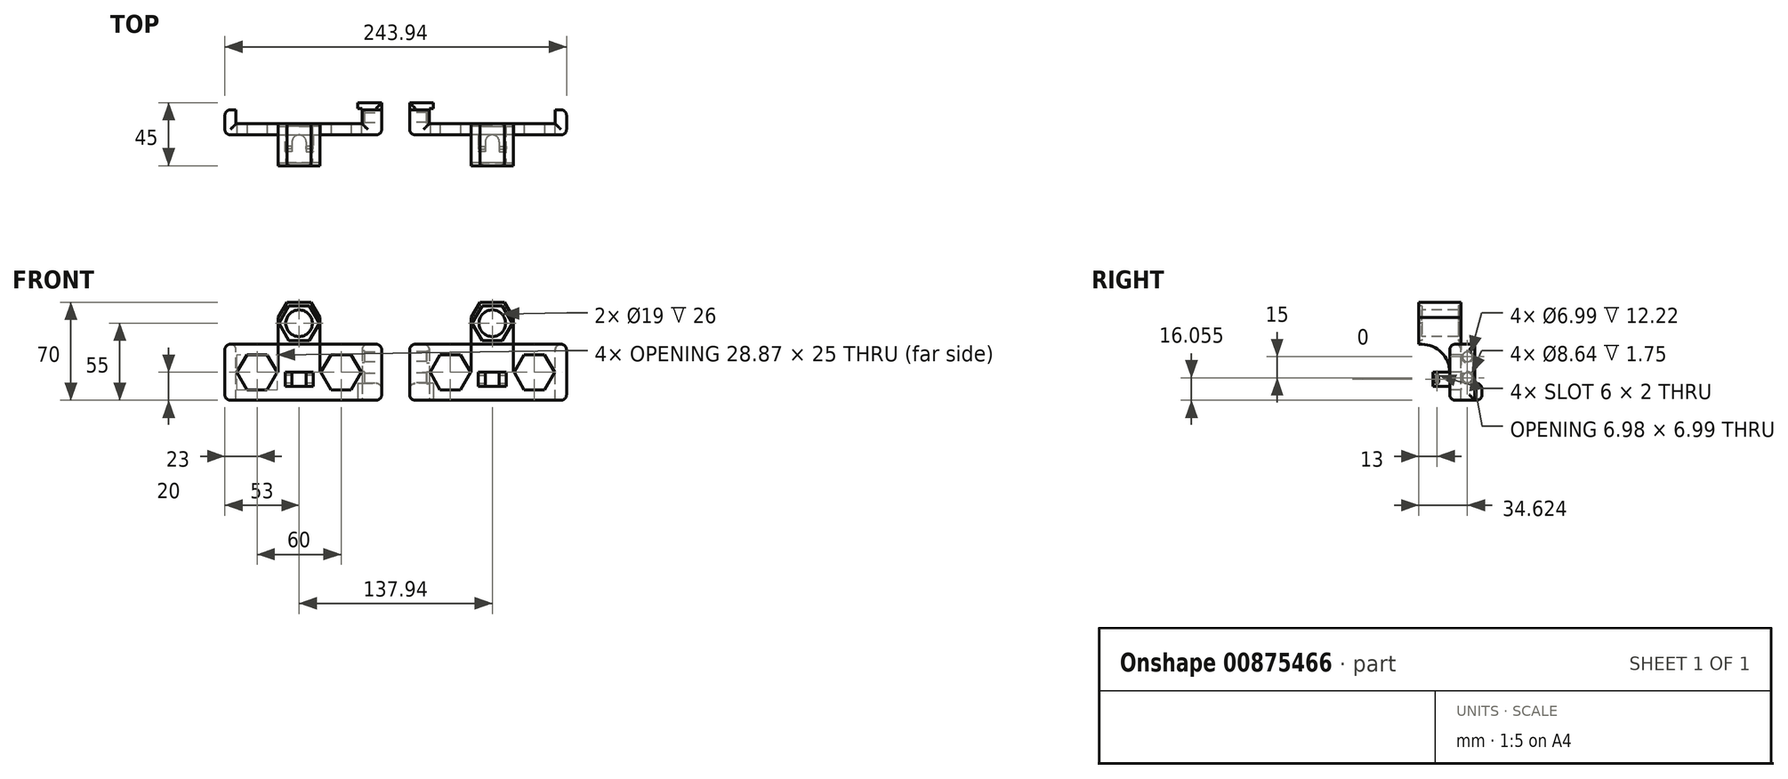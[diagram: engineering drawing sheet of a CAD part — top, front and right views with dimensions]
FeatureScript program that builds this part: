
annotation { "Feature Type Name" : "Feature", "Feature Type Description" : "" }
export const myFeature = defineFeature(function(context is Context, id is Id, definition is map)
    precondition{}
    {
        {
            var Q0;
            Q0=qCreatedBy(makeId("Front.planeOp"),FACE);
            var sketch = newSketch(context, id + "F0", { "sketchPlane" : qUnion([Q0])});
            skLineSegment(sketch, "E0.bottom", {"start": v(-53, 20) * mm, "end": v(53, 20) * mm});
            skLineSegment(sketch, "E0.top", {"start": v(-53, -20) * mm, "end": v(53, -20) * mm});
            skLineSegment(sketch, "E0.left", {"start": v(-53, 20) * mm, "end": v(-53, -20) * mm});
            skLineSegment(sketch, "E0.right", {"start": v(53, 20) * mm, "end": v(53, -20) * mm});
            skPoint(sketch, "E0.middle", {"position": v(0, 0) * mm});
            skSolve(sketch);
        }
        {
            var Q0;
            Q0=qSketchRegion(id+"F0",true);
            extrude(context, id + "F1", {"entities" : qUnion([Q0]), "depth" : 8 * mm, "offsetDistance" : 25 * mm});
        }
        {
            var Q0;
            Q0=makeQuery(id+"F1.opExtrude","CAP_FACE",FACE,{"disambiguationData":[OSD([sQuery(id+"F0.wireOp",EDGE,"E0.bottom"),sQuery(id+"F0.wireOp",EDGE,"E0.top"),sQuery(id+"F0.wireOp",EDGE,"E0.left"),sQuery(id+"F0.wireOp",EDGE,"E0.right")])],"isStart":true});
            var sketch = newSketch(context, id + "F2", { "sketchPlane" : qUnion([Q0])});
            skLineSegment(sketch, "E1.bottom", {"start": v(-53, 20) * mm, "end": v(-45, 20) * mm});
            skLineSegment(sketch, "E1.top", {"start": v(-53, -20) * mm, "end": v(-45, -20) * mm});
            skLineSegment(sketch, "E1.left", {"start": v(-53, 20) * mm, "end": v(-53, -20) * mm});
            skLineSegment(sketch, "E1.right", {"start": v(-45, 20) * mm, "end": v(-45, -20) * mm});
            skLineSegment(sketch, "E2.bottom", {"start": v(53, -20) * mm, "end": v(45, -20) * mm});
            skLineSegment(sketch, "E2.top", {"start": v(53, 20) * mm, "end": v(45, 20) * mm});
            skLineSegment(sketch, "E2.left", {"start": v(53, -20) * mm, "end": v(53, 20) * mm});
            skLineSegment(sketch, "E2.right", {"start": v(45, -20) * mm, "end": v(45, 20) * mm});
            skLineSegment(sketch, "E3.bottom", {"start": v(-53, 20) * mm, "end": v(-58.97, 20) * mm});
            skLineSegment(sketch, "E3.top", {"start": v(-53, -20) * mm, "end": v(-58.97, -20) * mm});
            skLineSegment(sketch, "E3.right", {"start": v(-58.97, 20) * mm, "end": v(-58.97, -20) * mm});
            skSolve(sketch);
        }
        {
            var Q0;
            Q0=qSketchRegion(id+"F2",true);
            extrude(context, id + "F3", {"entities" : qUnion([Q0]), "operationType" : NewBodyOperationType.ADD, "depth" : 10 * mm, "offsetDistance" : 25 * mm, "hasSecondDirection" : true, "secondDirectionOppositeDirection" : true, "secondDirectionDepth" : 8 * mm});
        }
        {
            var Q0;
            Q0=makeQuery(id+"F3.opExtrude","CAP_FACE",FACE,{"disambiguationData":[OSD([sQuery(id+"F2.wireOp",EDGE,"E1.bottom"),sQuery(id+"F2.wireOp",EDGE,"E1.top"),sQuery(id+"F2.wireOp",EDGE,"E1.left"),sQuery(id+"F2.wireOp",EDGE,"E1.right")])],"isStart":false});
            var sketch = newSketch(context, id + "F4", { "sketchPlane" : qUnion([Q0])});
            skLineSegment(sketch, "E4.bottom", {"start": v(-45, -20) * mm, "end": v(-58.97, -20) * mm});
            skLineSegment(sketch, "E4.top", {"start": v(-45, -8) * mm, "end": v(-58.97, -8) * mm});
            skLineSegment(sketch, "E4.left", {"start": v(-45, -20) * mm, "end": v(-45, -8) * mm});
            skLineSegment(sketch, "E4.right", {"start": v(-58.97, -20) * mm, "end": v(-58.97, -8) * mm});
            skSolve(sketch);
        }
        {
            var Q0;
            Q0=qSketchRegion(id+"F4",true);
            extrude(context, id + "F5", {"entities" : qUnion([Q0]), "operationType" : NewBodyOperationType.ADD, "depth" : 5 * mm, "offsetDistance" : 25 * mm});
        }
        {
            var Q0;
            Q0=makeQuery(id+"F5.boolean.opBoolean","MERGE",FACE,{"derivedFrom":[makeQuery(id+"F3.opExtrude","SWEPT_FACE",FACE,{"disambiguationData":[OSD([sQuery(id+"F2.wireOp",EDGE,"E1.right")])]}),makeQuery(id+"F5.opExtrude","SWEPT_FACE",FACE,{"disambiguationData":[OSD([sQuery(id+"F4.wireOp",EDGE,"E4.left")])]})]});
            var sketch = newSketch(context, id + "F6", { "sketchPlane" : qUnion([Q0])});
            skLineSegment(sketch, "E5.bottom", {"start": v(-15, -8) * mm, "end": v(-11, -8) * mm});
            skLineSegment(sketch, "E5.top", {"start": v(-15, -20) * mm, "end": v(-11, -20) * mm});
            skLineSegment(sketch, "E5.left", {"start": v(-15, -8) * mm, "end": v(-15, -20) * mm});
            skLineSegment(sketch, "E5.right", {"start": v(-11, -8) * mm, "end": v(-11, -20) * mm});
            skSolve(sketch);
        }
        {
            var Q0;
            Q0=qSketchRegion(id+"F6",true);
            extrude(context, id + "F7", {"entities" : qUnion([Q0]), "operationType" : NewBodyOperationType.ADD, "depth" : 3 * mm, "offsetDistance" : 25 * mm});
        }
        {
            var Q0;
            Q0=makeQuery(id+"F3.boolean.opBoolean","MERGE",FACE,{"derivedFrom":[makeQuery(id+"F1.opExtrude","SWEPT_FACE",FACE,{"disambiguationData":[OSD([sQuery(id+"F0.wireOp",EDGE,"E0.bottom")])]}),makeQuery(id+"F3.opExtrude","SWEPT_FACE",FACE,{"disambiguationData":[OSD([sQuery(id+"F2.wireOp",EDGE,"E1.bottom")])]}),makeQuery(id+"F3.opExtrude","SWEPT_FACE",FACE,{"disambiguationData":[OSD([sQuery(id+"F2.wireOp",EDGE,"E2.top")])]})]});
            var sketch = newSketch(context, id + "F8", { "sketchPlane" : qUnion([Q0])});
            skLineSegment(sketch, "E6.bottom", {"start": v(-15, 0) * mm, "end": v(15, 0) * mm});
            skLineSegment(sketch, "E6.top", {"start": v(-15, -8) * mm, "end": v(15, -8) * mm});
            skLineSegment(sketch, "E6.left", {"start": v(-15, 0) * mm, "end": v(-15, -8) * mm});
            skLineSegment(sketch, "E6.right", {"start": v(15, 0) * mm, "end": v(15, -8) * mm});
            skSolve(sketch);
        }
        {
            var Q0;
            Q0=qSketchRegion(id+"F8",true);
            extrude(context, id + "F9", {"entities" : qUnion([Q0]), "operationType" : NewBodyOperationType.ADD, "depth" : 30 * mm, "offsetDistance" : 25 * mm});
        }
        {
            var Q0;
            Q0=makeQuery(id+"F9.boolean.opBoolean","MERGE",FACE,{"derivedFrom":[makeQuery(id+"F1.opExtrude","CAP_FACE",FACE,{"disambiguationData":[OSD([sQuery(id+"F0.wireOp",EDGE,"E0.bottom"),sQuery(id+"F0.wireOp",EDGE,"E0.top"),sQuery(id+"F0.wireOp",EDGE,"E0.left"),sQuery(id+"F0.wireOp",EDGE,"E0.right")])],"isStart":true}),makeQuery(id+"F9.opExtrude","SWEPT_FACE",FACE,{"disambiguationData":[OSD([sQuery(id+"F8.wireOp",EDGE,"E6.bottom")])]})]});
            var sketch = newSketch(context, id + "F10", { "sketchPlane" : qUnion([Q0])});
            skLineSegment(sketch, "E7.bottom", {"start": v(-15, 50) * mm, "end": v(15, 50) * mm});
            skLineSegment(sketch, "E7.top", {"start": v(-15, 20) * mm, "end": v(15, 20) * mm});
            skLineSegment(sketch, "E7.left", {"start": v(-15, 50) * mm, "end": v(-15, 20) * mm});
            skLineSegment(sketch, "E7.right", {"start": v(15, 50) * mm, "end": v(15, 20) * mm});
            skSolve(sketch);
        }
        {
            var Q0;
            Q0=qSketchRegion(id+"F10",true);
            extrude(context, id + "F11", {"entities" : qUnion([Q0]), "operationType" : NewBodyOperationType.ADD, "oppositeDirection" : true, "depth" : 30 * mm, "offsetDistance" : 25 * mm});
        }
        {
            var Q0;
            Q0=makeQuery(id+"F11.opExtrude","CAP_FACE",FACE,{"disambiguationData":[OSD([sQuery(id+"F10.wireOp",EDGE,"E7.bottom"),sQuery(id+"F10.wireOp",EDGE,"E7.top"),sQuery(id+"F10.wireOp",EDGE,"E7.left"),sQuery(id+"F10.wireOp",EDGE,"E7.right")])],"isStart":false});
            var sketch = newSketch(context, id + "F12", { "sketchPlane" : qUnion([Q0])});
            skLineSegment(sketch, "E8", {"start": v(-15, 35) * mm, "end": v(15, 35) * mm, "construction": true});
            skLineSegment(sketch, "E9", {"start": v(0, 50) * mm, "end": v(0, 20) * mm, "construction": true});
            skCircle(sketch, "E10", {"center": v(0, 35) * mm, "radius": 9.5 * mm});
            skSolve(sketch);
        }
        {
            var Q0;
            Q0=qSketchRegion(id+"F12",true);
            extrude(context, id + "F13", {"entities" : qUnion([Q0]), "operationType" : NewBodyOperationType.REMOVE, "endBound" : BoundingType.THROUGH_ALL, "oppositeDirection" : true, "depth" : 25 * mm, "offsetDistance" : 25 * mm});
        }
        {
            var Q0;
            Q0=makeQuery(id+"F9.boolean.opBoolean","MERGE",FACE,{"derivedFrom":[makeQuery(id+"F1.opExtrude","CAP_FACE",FACE,{"disambiguationData":[OSD([sQuery(id+"F0.wireOp",EDGE,"E0.bottom"),sQuery(id+"F0.wireOp",EDGE,"E0.top"),sQuery(id+"F0.wireOp",EDGE,"E0.left"),sQuery(id+"F0.wireOp",EDGE,"E0.right")])],"isStart":true}),makeQuery(id+"F9.opExtrude","SWEPT_FACE",FACE,{"disambiguationData":[OSD([sQuery(id+"F8.wireOp",EDGE,"E6.bottom")])]})]});
            var sketch = newSketch(context, id + "F14", { "sketchPlane" : qUnion([Q0])});
            skCircle(sketch, "E11.cCircle", {"center": v(0, 35) * mm, "radius": 12.62 * mm, "construction": true});
            skLineSegment(sketch, "E11.0", {"start": v(-7.29, 47.63) * mm, "end": v(7.29, 47.63) * mm});
            skLineSegment(sketch, "E11.1", {"start": v(7.29, 47.63) * mm, "end": v(14.58, 35) * mm});
            skLineSegment(sketch, "E11.2", {"start": v(14.58, 35) * mm, "end": v(7.29, 22.38) * mm});
            skLineSegment(sketch, "E11.3", {"start": v(7.29, 22.38) * mm, "end": v(-7.29, 22.38) * mm});
            skLineSegment(sketch, "E11.4", {"start": v(-7.29, 22.38) * mm, "end": v(-14.58, 35) * mm});
            skLineSegment(sketch, "E11.5", {"start": v(-14.58, 35) * mm, "end": v(-7.29, 47.63) * mm});
            skPoint(sketch, "E11.0.midPoint", {"position": v(0, 47.63) * mm});
            skSolve(sketch);
        }
        {
            var Q0;
            Q0=qSketchRegion(id+"F14",true);
            extrude(context, id + "F15", {"entities" : qUnion([Q0]), "operationType" : NewBodyOperationType.REMOVE, "oppositeDirection" : true, "depth" : 2 * mm, "offsetDistance" : 25 * mm});
        }
        {
            var Q0;
            Q0=makeQuery(id+"F9.boolean.opBoolean","MERGE",FACE,{"derivedFrom":[makeQuery(id+"F1.opExtrude","CAP_FACE",FACE,{"disambiguationData":[OSD([sQuery(id+"F0.wireOp",EDGE,"E0.bottom"),sQuery(id+"F0.wireOp",EDGE,"E0.top"),sQuery(id+"F0.wireOp",EDGE,"E0.left"),sQuery(id+"F0.wireOp",EDGE,"E0.right")])],"isStart":true}),makeQuery(id+"F9.opExtrude","SWEPT_FACE",FACE,{"disambiguationData":[OSD([sQuery(id+"F8.wireOp",EDGE,"E6.bottom")])]})]});
            var sketch = newSketch(context, id + "F16", { "sketchPlane" : qUnion([Q0])});
            skLineSegment(sketch, "E12", {"start": v(-15, 39.02) * mm, "end": v(-8.66, 50) * mm});
            skLineSegment(sketch, "E13", {"start": v(-8.66, 50) * mm, "end": v(8.66, 50) * mm});
            skLineSegment(sketch, "E14", {"start": v(8.66, 50) * mm, "end": v(15, 39.02) * mm});
            skLineSegment(sketch, "E15", {"start": v(15, 39.02) * mm, "end": v(19.55, 39.02) * mm});
            skLineSegment(sketch, "E16", {"start": v(19.55, 39.02) * mm, "end": v(19.55, 53.1) * mm});
            skLineSegment(sketch, "E17", {"start": v(19.55, 53.1) * mm, "end": v(-19, 53.1) * mm});
            skLineSegment(sketch, "E18", {"start": v(-19, 53.1) * mm, "end": v(-19, 39.02) * mm});
            skLineSegment(sketch, "E19", {"start": v(-19, 39.02) * mm, "end": v(-15, 39.02) * mm});
            skLineSegment(sketch, "E20", {"start": v(-11.83, 44.5) * mm, "end": v(-9.77, 43.32) * mm, "construction": true});
            skLineSegment(sketch, "E21", {"start": v(0, 50) * mm, "end": v(0, 47.63) * mm, "construction": true});
            skLineSegment(sketch, "E22", {"start": v(11.83, 44.5) * mm, "end": v(9.77, 43.32) * mm, "construction": true});
            skSolve(sketch);
        }
        {
            var Q0;
            Q0=qSketchRegion(id+"F16",true);
            extrude(context, id + "F17", {"entities" : qUnion([Q0]), "operationType" : NewBodyOperationType.REMOVE, "endBound" : BoundingType.THROUGH_ALL, "oppositeDirection" : true, "depth" : 25 * mm, "offsetDistance" : 25 * mm});
        }
        {
            var Q0;
            Q0=makeQuery(id+"F11.opExtrude","CAP_FACE",FACE,{"disambiguationData":[OSD([sQuery(id+"F10.wireOp",EDGE,"E7.bottom"),sQuery(id+"F10.wireOp",EDGE,"E7.top"),sQuery(id+"F10.wireOp",EDGE,"E7.left"),sQuery(id+"F10.wireOp",EDGE,"E7.right")])],"isStart":false});
            var sketch = newSketch(context, id + "F18", { "sketchPlane" : qUnion([Q0])});
            skCircle(sketch, "E23.cCircle", {"center": v(0, 35) * mm, "radius": 12.5 * mm, "construction": true});
            skLineSegment(sketch, "E23.0", {"start": v(-7.22, 47.5) * mm, "end": v(7.22, 47.5) * mm});
            skLineSegment(sketch, "E23.1", {"start": v(7.22, 47.5) * mm, "end": v(14.43, 35) * mm});
            skLineSegment(sketch, "E23.2", {"start": v(14.43, 35) * mm, "end": v(7.22, 22.5) * mm});
            skLineSegment(sketch, "E23.3", {"start": v(7.22, 22.5) * mm, "end": v(-7.22, 22.5) * mm});
            skLineSegment(sketch, "E23.4", {"start": v(-7.22, 22.5) * mm, "end": v(-14.43, 35) * mm});
            skLineSegment(sketch, "E23.5", {"start": v(-14.43, 35) * mm, "end": v(-7.22, 47.5) * mm});
            skPoint(sketch, "E23.0.midPoint", {"position": v(0, 47.5) * mm});
            skSolve(sketch);
        }
        {
            var Q0;
            Q0=qSketchRegion(id+"F18",true);
            extrude(context, id + "F19", {"entities" : qUnion([Q0]), "operationType" : NewBodyOperationType.REMOVE, "oppositeDirection" : true, "depth" : 2 * mm, "offsetDistance" : 25 * mm});
        }
        {
            var Q0;
            Q0=makeQuery(id+"F11.boolean.opBoolean","INTERSECT",EDGE,{"derivedFrom":[makeQuery(id+"F9.boolean.opBoolean","MERGE",FACE,{"derivedFrom":[makeQuery(id+"F1.opExtrude","CAP_FACE",FACE,{"disambiguationData":[OSD([sQuery(id+"F0.wireOp",EDGE,"E0.bottom"),sQuery(id+"F0.wireOp",EDGE,"E0.top"),sQuery(id+"F0.wireOp",EDGE,"E0.left"),sQuery(id+"F0.wireOp",EDGE,"E0.right")])],"isStart":false}),makeQuery(id+"F9.opExtrude","SWEPT_FACE",FACE,{"disambiguationData":[OSD([sQuery(id+"F8.wireOp",EDGE,"E6.top")])]})]}),makeQuery(id+"F11.opExtrude","SWEPT_FACE",FACE,{"disambiguationData":[OSD([sQuery(id+"F10.wireOp",EDGE,"E7.top")])]})]});
            fillet(context, id + "F20", {"entities" : qUnion([Q0]), "radius" : 20 * mm, "tangentPropagation" : true, "allowEdgeOverflow" : false});
        }
        {
            var Q0;
            {var subQ0=sQuery(id+"F0.wireOp",EDGE,"E0.right");var subQ1=sQuery(id+"F0.wireOp",EDGE,"E0.bottom");Q0=makeQuery(id+"F9.boolean.opBoolean","SPLIT",EDGE,{"disambiguationData":[TD([makeQuery(id+"F1.opExtrude","SWEPT_FACE",FACE,{"disambiguationData":[OSD([subQ0])]})])],"derivedFrom":makeQuery(id+"F1.opExtrude","CAP_EDGE",EDGE,{"disambiguationData":[OSD([subQ1])],"isStart":false})});}
            var Q1;
            {var subQ0=sQuery(id+"F0.wireOp",EDGE,"E0.bottom");Q1=makeQuery(id+"F9.boolean.opBoolean","SPLIT",EDGE,{"disambiguationData":[TD([makeQuery(id+"F3.opExtrude","SWEPT_FACE",FACE,{"disambiguationData":[OSD([sQuery(id+"F2.wireOp",EDGE,"E1.right")])]})])],"derivedFrom":makeQuery(id+"F1.opExtrude","CAP_EDGE",EDGE,{"disambiguationData":[OSD([subQ0])],"isStart":true})});}
            var Q2;
            {var subQ0=sQuery(id+"F0.wireOp",EDGE,"E0.bottom");Q2=makeQuery(id+"F9.boolean.opBoolean","SPLIT",EDGE,{"disambiguationData":[TD([makeQuery(id+"F3.opExtrude","SWEPT_FACE",FACE,{"disambiguationData":[OSD([sQuery(id+"F2.wireOp",EDGE,"E2.right")])]})])],"derivedFrom":makeQuery(id+"F1.opExtrude","CAP_EDGE",EDGE,{"disambiguationData":[OSD([subQ0])],"isStart":true})});}
            var Q3;
            Q3=makeQuery(id+"F1.opExtrude","CAP_EDGE",EDGE,{"disambiguationData":[OSD([sQuery(id+"F0.wireOp",EDGE,"E0.left")])],"isStart":false});
            var Q4;
            Q4=makeQuery(id+"F1.opExtrude","CAP_EDGE",EDGE,{"disambiguationData":[OSD([sQuery(id+"F0.wireOp",EDGE,"E0.right")])],"isStart":false});
            var Q5;
            Q5=makeQuery(id+"F5.opExtrude","SWEPT_EDGE",EDGE,{"disambiguationData":[OSD([sQuery(id+"F2.wireOp",EDGE,"E1.left"),sQuery(id+"F4.wireOp",EDGE,"E4.top"),sQuery(id+"F4.wireOp",EDGE,"E4.right")])]});
            var Q6;
            Q6=makeQuery(id+"F7.boolean.opBoolean","MERGE",EDGE,{"derivedFrom":[makeQuery(id+"F5.opExtrude","CAP_EDGE",EDGE,{"disambiguationData":[OSD([sQuery(id+"F4.wireOp",EDGE,"E4.top")])],"isStart":false}),makeQuery(id+"F7.opExtrude","SWEPT_EDGE",EDGE,{"disambiguationData":[OSD([sQuery(id+"F6.wireOp",EDGE,"E5.bottom"),sQuery(id+"F6.wireOp",EDGE,"E5.left")])]})]});
            var Q7;
            Q7=makeQuery(id+"F7.boolean.opBoolean","MERGE",EDGE,{"derivedFrom":[makeQuery(id+"F5.opExtrude","CAP_EDGE",EDGE,{"disambiguationData":[OSD([sQuery(id+"F4.wireOp",EDGE,"E4.bottom")])],"isStart":false}),makeQuery(id+"F7.opExtrude","SWEPT_EDGE",EDGE,{"disambiguationData":[OSD([sQuery(id+"F6.wireOp",EDGE,"E5.top"),sQuery(id+"F6.wireOp",EDGE,"E5.left")])]})]});
            var Q8;
            Q8=makeQuery(id+"F3.opExtrude","CAP_EDGE",EDGE,{"disambiguationData":[OSD([sQuery(id+"F2.wireOp",EDGE,"E3.right")])],"isStart":true});
            var Q9;
            Q9=makeQuery(id+"F3.opExtrude","SWEPT_EDGE",EDGE,{"disambiguationData":[OSD([sQuery(id+"F2.wireOp",EDGE,"E3.bottom"),sQuery(id+"F2.wireOp",EDGE,"E3.right")])]});
            var Q10;
            {var subQ0=sQuery(id+"F2.wireOp",EDGE,"E3.right");var subQ1=sQuery(id+"F2.wireOp",EDGE,"E3.bottom");var subQ2=sQuery(id+"F2.wireOp",EDGE,"E1.bottom");var subQ3=sQuery(id+"F0.wireOp",EDGE,"E0.bottom");Q10=makeQuery(id+"F9.boolean.opBoolean","SPLIT",EDGE,{"disambiguationData":[TD([makeQuery(id+"F3.opExtrude","SWEPT_FACE",FACE,{"disambiguationData":[OSD([subQ0])]})])],"derivedFrom":makeQuery(id+"F3.boolean.opBoolean","MERGE",EDGE,{"derivedFrom":[makeQuery(id+"F1.opExtrude","CAP_EDGE",EDGE,{"disambiguationData":[OSD([subQ3])],"isStart":false}),makeQuery(id+"F3.opExtrude","CAP_EDGE",EDGE,{"disambiguationData":[OSD([subQ2,subQ1])],"isStart":true})]})});}
            var Q11;
            Q11=makeQuery(id+"F3.opExtrude","CAP_EDGE",EDGE,{"disambiguationData":[OSD([sQuery(id+"F2.wireOp",EDGE,"E2.left")])],"isStart":false});
            var Q12;
            {var subQ0=sQuery(id+"F2.wireOp",EDGE,"E3.bottom");var subQ1=sQuery(id+"F2.wireOp",EDGE,"E1.bottom");var subQ2=sQuery(id+"F0.wireOp",EDGE,"E0.left");var subQ3=sQuery(id+"F0.wireOp",EDGE,"E0.bottom");Q12=makeQuery(id+"F9.boolean.opBoolean","SPLIT",EDGE,{"disambiguationData":[TD([makeQuery(id+"F1.opExtrude","SWEPT_FACE",FACE,{"disambiguationData":[OSD([subQ2])]})])],"derivedFrom":makeQuery(id+"F3.boolean.opBoolean","MERGE",EDGE,{"derivedFrom":[makeQuery(id+"F1.opExtrude","CAP_EDGE",EDGE,{"disambiguationData":[OSD([subQ3])],"isStart":false}),makeQuery(id+"F3.opExtrude","CAP_EDGE",EDGE,{"disambiguationData":[OSD([subQ1,subQ0])],"isStart":true})]})});}
            var Q13;
            Q13=makeQuery(id+"F3.opExtrude","SWEPT_EDGE",EDGE,{"disambiguationData":[OSD([sQuery(id+"F0.wireOp",EDGE,"E0.bottom"),sQuery(id+"F2.wireOp",EDGE,"E2.top"),sQuery(id+"F2.wireOp",EDGE,"E2.right")])]});
            var Q14;
            Q14=makeQuery(id+"F3.boolean.opBoolean","MERGE",EDGE,{"derivedFrom":[makeQuery(id+"F1.opExtrude","SWEPT_EDGE",EDGE,{"disambiguationData":[OSD([sQuery(id+"F0.wireOp",EDGE,"E0.bottom"),sQuery(id+"F0.wireOp",EDGE,"E0.left")])]}),makeQuery(id+"F3.opExtrude","SWEPT_EDGE",EDGE,{"disambiguationData":[OSD([sQuery(id+"F2.wireOp",EDGE,"E2.top"),sQuery(id+"F2.wireOp",EDGE,"E2.left")])]})]});
            var Q15;
            Q15=makeQuery(id+"F3.opExtrude","SWEPT_EDGE",EDGE,{"disambiguationData":[OSD([sQuery(id+"F0.wireOp",EDGE,"E0.bottom"),sQuery(id+"F2.wireOp",EDGE,"E1.bottom"),sQuery(id+"F2.wireOp",EDGE,"E1.right")])]});
            var Q16;
            Q16=makeQuery(id+"F3.boolean.opBoolean","MERGE",EDGE,{"derivedFrom":[makeQuery(id+"F1.opExtrude","CAP_EDGE",EDGE,{"disambiguationData":[OSD([sQuery(id+"F0.wireOp",EDGE,"E0.top")])],"isStart":false}),makeQuery(id+"F3.opExtrude","CAP_EDGE",EDGE,{"disambiguationData":[OSD([sQuery(id+"F2.wireOp",EDGE,"E1.top"),sQuery(id+"F2.wireOp",EDGE,"E3.top")])],"isStart":true})]});
            var Q17;
            Q17=makeQuery(id+"F3.boolean.opBoolean","MERGE",EDGE,{"derivedFrom":[makeQuery(id+"F1.opExtrude","SWEPT_EDGE",EDGE,{"disambiguationData":[OSD([sQuery(id+"F0.wireOp",EDGE,"E0.top"),sQuery(id+"F0.wireOp",EDGE,"E0.left")])]}),makeQuery(id+"F3.opExtrude","SWEPT_EDGE",EDGE,{"disambiguationData":[OSD([sQuery(id+"F2.wireOp",EDGE,"E2.bottom"),sQuery(id+"F2.wireOp",EDGE,"E2.left")])]})]});
            var Q18;
            Q18=makeQuery(id+"F5.boolean.opBoolean","MERGE",EDGE,{"derivedFrom":[makeQuery(id+"F3.opExtrude","SWEPT_EDGE",EDGE,{"disambiguationData":[OSD([sQuery(id+"F2.wireOp",EDGE,"E3.top"),sQuery(id+"F2.wireOp",EDGE,"E3.right")])]}),makeQuery(id+"F5.opExtrude","SWEPT_EDGE",EDGE,{"disambiguationData":[OSD([sQuery(id+"F4.wireOp",EDGE,"E4.bottom"),sQuery(id+"F4.wireOp",EDGE,"E4.right")])]})]});
            fillet(context, id + "F21", {"entities" : qUnion([Q0, Q1, Q2, Q3, Q4, Q5, Q6, Q7, Q8, Q9, Q10, Q11, Q12, Q13, Q14, Q15, Q16, Q17, Q18]), "radius" : 4 * mm, "tangentPropagation" : true, "allowEdgeOverflow" : false});
        }
        {
            var Q0;
            Q0=makeQuery(id+"F11.opExtrude","SWEPT_FACE",FACE,{"disambiguationData":[OSD([sQuery(id+"F10.wireOp",EDGE,"E7.top")])]});
            cPlane(context, id + "F22", {"entities" : qUnion([Q0]), "cplaneType" : CPlaneType.OFFSET, "offset" : 20 * mm, "width" : 150 * mm, "height" : 150 * mm});
        }
        {
            var Q0;
            Q0=qCreatedBy(id+"F22.planeOp",FACE);
            var sketch = newSketch(context, id + "F23", { "sketchPlane" : qUnion([Q0])});
            skLineSegment(sketch, "E24.left", {"start": v(-10, 20) * mm, "end": v(-10, 8) * mm});
            skCircle(sketch, "E25", {"center": v(0, 13) * mm, "radius": 5 * mm, "construction": true});
            skLineSegment(sketch, "E26", {"start": v(-5, 13) * mm, "end": v(-5, 20) * mm});
            skLineSegment(sketch, "E27", {"start": v(5, 13) * mm, "end": v(5, 20) * mm});
            skArc(sketch, "E28", {"start": v(-5, 13) * mm, "mid": v(0, 8) * mm, "end": v(5, 13) * mm});
            skLineSegment(sketch, "E29", {"start": v(-5, 20) * mm, "end": v(-10, 20) * mm});
            skLineSegment(sketch, "E30", {"start": v(5, 20) * mm, "end": v(10, 20) * mm});
            skLineSegment(sketch, "E31", {"start": v(-10, 8) * mm, "end": v(10, 8) * mm});
            skLineSegment(sketch, "E32", {"start": v(10, 8) * mm, "end": v(10, 20) * mm});
            skSolve(sketch);
        }
        {
            var Q0;
            Q0=qSketchRegion(id+"F23",true);
            extrude(context, id + "F24", {"entities" : qUnion([Q0]), "operationType" : NewBodyOperationType.ADD, "depth" : 10 * mm, "offsetDistance" : 25 * mm});
        }
        {
            var Q0;
            Q0=makeQuery(id+"F24.opExtrude","SWEPT_FACE",FACE,{"disambiguationData":[OSD([sQuery(id+"F23.wireOp",EDGE,"E24.left")])]});
            var sketch = newSketch(context, id + "F25", { "sketchPlane" : qUnion([Q0])});
            skLineSegment(sketch, "E33.bottom", {"start": v(18, -3) * mm, "end": v(16, -3) * mm});
            skLineSegment(sketch, "E33.top", {"start": v(18, -7) * mm, "end": v(16, -7) * mm});
            skLineSegment(sketch, "E33.left", {"start": v(18, -3) * mm, "end": v(18, -7) * mm});
            skLineSegment(sketch, "E33.right", {"start": v(16, -3) * mm, "end": v(16, -7) * mm});
            skArc(sketch, "E34", {"start": v(18, -3) * mm, "mid": v(17, -2) * mm, "end": v(16, -3) * mm});
            skArc(sketch, "E35", {"start": v(16, -7) * mm, "mid": v(17, -8) * mm, "end": v(18, -7) * mm});
            skPoint(sketch, "E36", {"position": v(18, -5) * mm});
            skPoint(sketch, "E37", {"position": v(20, -5) * mm});
            skSolve(sketch);
        }
        {
            var Q0;
            Q0=qSketchRegion(id+"F25",true);
            extrude(context, id + "F26", {"entities" : qUnion([Q0]), "operationType" : NewBodyOperationType.REMOVE, "endBound" : BoundingType.THROUGH_ALL, "oppositeDirection" : true, "depth" : 25 * mm, "offsetDistance" : 25 * mm});
        }
        {
            var Q0;
            Q0=makeQuery(id+"F5.boolean.opBoolean","MERGE",FACE,{"derivedFrom":[makeQuery(id+"F3.boolean.opBoolean","MERGE",FACE,{"derivedFrom":[makeQuery(id+"F1.opExtrude","SWEPT_FACE",FACE,{"disambiguationData":[OSD([sQuery(id+"F0.wireOp",EDGE,"E0.right")])]}),makeQuery(id+"F3.opExtrude","SWEPT_FACE",FACE,{"disambiguationData":[OSD([sQuery(id+"F2.wireOp",EDGE,"E1.left")])]})]}),makeQuery(id+"F5.opExtrude","SWEPT_FACE",FACE,{"disambiguationData":[OSD([sQuery(id+"F4.wireOp",EDGE,"E4.right")])]})]});
            var sketch = newSketch(context, id + "F27", { "sketchPlane" : qUnion([Q0])});
            skCircle(sketch, "E38", {"center": v(4.62, 11.06) * mm, "radius": 3.5 * mm});
            skCircle(sketch, "E39", {"center": v(4.62, -3.94) * mm, "radius": 3.5 * mm});
            skLineSegment(sketch, "E40", {"start": v(4.62, 11.06) * mm, "end": v(4.62, -3.94) * mm, "construction": true});
            skPoint(sketch, "E41", {"position": v(4.62, 3.56) * mm});
            skSolve(sketch);
        }
        {
            var Q0;
            Q0=qSketchRegion(id+"F27",true);
            extrude(context, id + "F28", {"entities" : qUnion([Q0]), "operationType" : NewBodyOperationType.REMOVE, "oppositeDirection" : true, "depth" : 13.23 * mm, "offsetDistance" : 25 * mm});
        }
        {
            var Q0;
            Q0=makeQuery(id+"F5.boolean.opBoolean","MERGE",FACE,{"derivedFrom":[makeQuery(id+"F3.opExtrude","SWEPT_FACE",FACE,{"disambiguationData":[OSD([sQuery(id+"F2.wireOp",EDGE,"E1.right")])]}),makeQuery(id+"F5.opExtrude","SWEPT_FACE",FACE,{"disambiguationData":[OSD([sQuery(id+"F4.wireOp",EDGE,"E4.left")])]})]});
            var sketch = newSketch(context, id + "F29", { "sketchPlane" : qUnion([Q0])});
            skCircle(sketch, "E42", {"center": v(-4.62, 11.06) * mm, "radius": 4.32 * mm});
            skCircle(sketch, "E43", {"center": v(-4.62, -3.94) * mm, "radius": 4.32 * mm});
            skSolve(sketch);
        }
        {
            var Q0;
            Q0=qSketchRegion(id+"F29",true);
            extrude(context, id + "F30", {"entities" : qUnion([Q0]), "operationType" : NewBodyOperationType.REMOVE, "oppositeDirection" : true, "depth" : 1.75 * mm, "offsetDistance" : 25 * mm});
        }
        {
            var Q0;
            Q0=makeQuery(id+"F9.boolean.opBoolean","MERGE",FACE,{"derivedFrom":[makeQuery(id+"F3.boolean.opBoolean","MERGE",FACE,{"derivedFrom":[makeQuery(id+"F1.opExtrude","CAP_FACE",FACE,{"disambiguationData":[OSD([sQuery(id+"F0.wireOp",EDGE,"E0.bottom"),sQuery(id+"F0.wireOp",EDGE,"E0.top"),sQuery(id+"F0.wireOp",EDGE,"E0.left"),sQuery(id+"F0.wireOp",EDGE,"E0.right")])],"isStart":false}),makeQuery(id+"F3.opExtrude","CAP_FACE",FACE,{"disambiguationData":[OSD([sQuery(id+"F2.wireOp",EDGE,"E1.bottom"),sQuery(id+"F2.wireOp",EDGE,"E1.top"),sQuery(id+"F2.wireOp",EDGE,"E1.right"),sQuery(id+"F2.wireOp",EDGE,"E3.bottom"),sQuery(id+"F2.wireOp",EDGE,"E3.top"),sQuery(id+"F2.wireOp",EDGE,"E3.right")])],"isStart":true})]}),makeQuery(id+"F9.opExtrude","SWEPT_FACE",FACE,{"disambiguationData":[OSD([sQuery(id+"F8.wireOp",EDGE,"E6.top")])]})]});
            var sketch = newSketch(context, id + "F31", { "sketchPlane" : qUnion([Q0])});
            skCircle(sketch, "E44.cCircle", {"center": v(-30, 0) * mm, "radius": 12.5 * mm, "construction": true});
            skLineSegment(sketch, "E44.0", {"start": v(-37.22, 12.5) * mm, "end": v(-22.78, 12.5) * mm});
            skLineSegment(sketch, "E44.1", {"start": v(-22.78, 12.5) * mm, "end": v(-15.57, 0) * mm});
            skLineSegment(sketch, "E44.2", {"start": v(-15.57, 0) * mm, "end": v(-22.78, -12.5) * mm});
            skLineSegment(sketch, "E44.3", {"start": v(-22.78, -12.5) * mm, "end": v(-37.22, -12.5) * mm});
            skLineSegment(sketch, "E44.4", {"start": v(-37.22, -12.5) * mm, "end": v(-44.43, 0) * mm});
            skLineSegment(sketch, "E44.5", {"start": v(-44.43, 0) * mm, "end": v(-37.22, 12.5) * mm});
            skPoint(sketch, "E44.0.midPoint", {"position": v(-30, 12.5) * mm});
            skCircle(sketch, "E45.cCircle", {"center": v(30, 0) * mm, "radius": 12.5 * mm, "construction": true});
            skLineSegment(sketch, "E45.0", {"start": v(22.78, 12.5) * mm, "end": v(37.22, 12.5) * mm});
            skLineSegment(sketch, "E45.1", {"start": v(37.22, 12.5) * mm, "end": v(44.43, 0) * mm});
            skLineSegment(sketch, "E45.2", {"start": v(44.43, 0) * mm, "end": v(37.22, -12.5) * mm});
            skLineSegment(sketch, "E45.3", {"start": v(37.22, -12.5) * mm, "end": v(22.78, -12.5) * mm});
            skLineSegment(sketch, "E45.4", {"start": v(22.78, -12.5) * mm, "end": v(15.57, 0) * mm});
            skLineSegment(sketch, "E45.5", {"start": v(15.57, 0) * mm, "end": v(22.78, 12.5) * mm});
            skPoint(sketch, "E45.0.midPoint", {"position": v(30, 12.5) * mm});
            skLineSegment(sketch, "E46", {"start": v(0, 0) * mm, "end": v(-30, 0) * mm, "construction": true});
            skLineSegment(sketch, "E47", {"start": v(0, 0) * mm, "end": v(30, 0) * mm, "construction": true});
            skSolve(sketch);
        }
        {
            var Q0;
            Q0=qSketchRegion(id+"F31",true);
            extrude(context, id + "F32", {"entities" : qUnion([Q0]), "operationType" : NewBodyOperationType.REMOVE, "endBound" : BoundingType.THROUGH_ALL, "oppositeDirection" : true, "depth" : 25 * mm, "offsetDistance" : 25 * mm});
        }
        {
            var Q0;
            Q0=makeQuery(id+"F5.boolean.opBoolean","MERGE",FACE,{"derivedFrom":[makeQuery(id+"F3.opExtrude","SWEPT_FACE",FACE,{"disambiguationData":[OSD([sQuery(id+"F2.wireOp",EDGE,"E3.right")])]}),makeQuery(id+"F5.opExtrude","SWEPT_FACE",FACE,{"disambiguationData":[OSD([sQuery(id+"F4.wireOp",EDGE,"E4.right")])]})]});
            cPlane(context, id + "F33", {"entities" : qUnion([Q0]), "cplaneType" : CPlaneType.OFFSET, "offset" : 10 * mm, "width" : 150 * mm, "height" : 150 * mm});
        }
        {
            var Q0;
            Q0=makeQuery(id+"F1.opExtrude","SWEPT_BODY",BODY,{"disambiguationData":[OSD([sQuery(id+"F0.wireOp",EDGE,"E0.bottom"),sQuery(id+"F0.wireOp",EDGE,"E0.top"),sQuery(id+"F0.wireOp",EDGE,"E0.left"),sQuery(id+"F0.wireOp",EDGE,"E0.right")])]});
            var Q1;
            Q1=qCreatedBy(id+"F33.planeOp",FACE);
            mirror(context, id + "F34", {"entities" : qUnion([Q0]), "mirrorPlane" : qUnion([Q1])});
        }
    });
